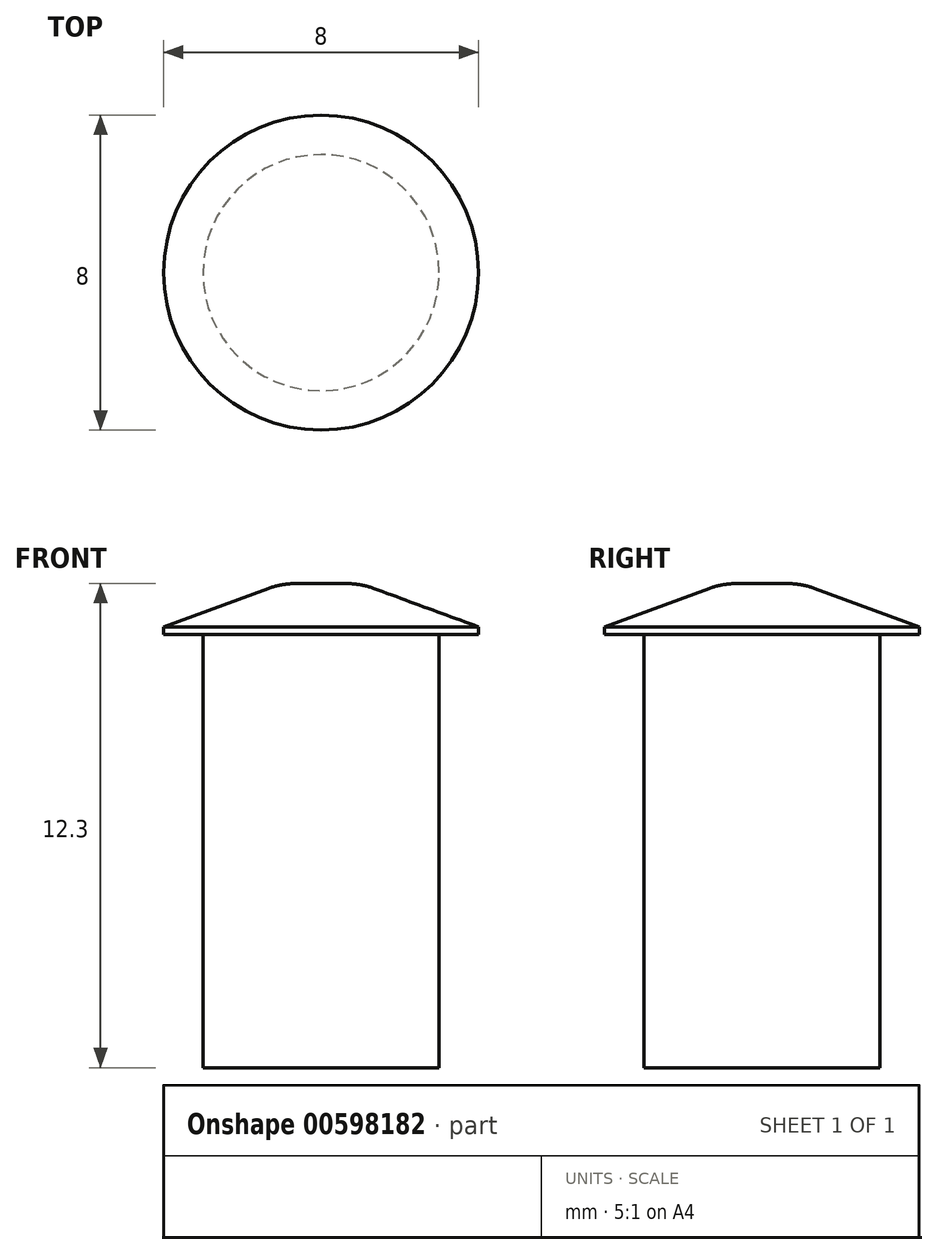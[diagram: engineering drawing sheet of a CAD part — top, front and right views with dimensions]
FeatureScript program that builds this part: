
annotation { "Feature Type Name" : "Feature", "Feature Type Description" : "" }
export const myFeature = defineFeature(function(context is Context, id is Id, definition is map)
    precondition{}
    {
        {
            var Q0;
            Q0=qCreatedBy(makeId("Top.planeOp"),FACE);
            var sketch = newSketch(context, id + "F0", { "sketchPlane" : qUnion([Q0])});
            skCircle(sketch, "E0", {"center": v(0, 0) * mm, "radius": 3 * mm});
            skSolve(sketch);
        }
        {
            var Q0;
            Q0 = qSketchRegion(id + "F0", true);
            extrude(context, id + "F1", {"entities" : qUnion([Q0]), "depth" : 11 * mm, "offsetDistance" : 25 * mm});
        }
        {
            var Q0;
            Q0=makeQuery(id+"F1.opExtrude","CAP_FACE",FACE,{"disambiguationData":[OSD([sQuery(id+"F0.wireOp",EDGE,"E0")])],"isStart":false});
            var sketch = newSketch(context, id + "F2", { "sketchPlane" : qUnion([Q0])});
            skCircle(sketch, "E1", {"center": v(0, 0) * mm, "radius": 4 * mm});
            skSolve(sketch);
        }
        {
            var Q0;
            Q0 = qSketchRegion(id + "F2", true);
            extrude(context, id + "F3", {"entities" : qUnion([Q0]), "operationType" : NewBodyOperationType.ADD, "depth" : 1.3 * mm, "offsetDistance" : 25 * mm});
        }
        {
            var Q0;
            Q0=makeQuery(id+"F3.opExtrude","CAP_FACE",FACE,{"disambiguationData":[OSD([sQuery(id+"F2.wireOp",EDGE,"E1")])],"isStart":false});
            chamfer(context, id + "F4", {"entities" : qUnion([Q0]), "chamferType" : ChamferType.TWO_OFFSETS, "width1" : 3 * mm, "oppositeDirection" : false, "width2" : 1.1 * mm, "tangentPropagation" : true});
        }
        {
            var Q0;
            Q0=makeQuery(id+"F3.opExtrude","CAP_FACE",FACE,{"disambiguationData":[OSD([sQuery(id+"F2.wireOp",EDGE,"E1")])],"isStart":false});
            fillet(context, id + "F5", {"entities" : qUnion([Q0]), "radius" : 2 * mm, "tangentPropagation" : true, "allowEdgeOverflow" : false});
        }
    });
